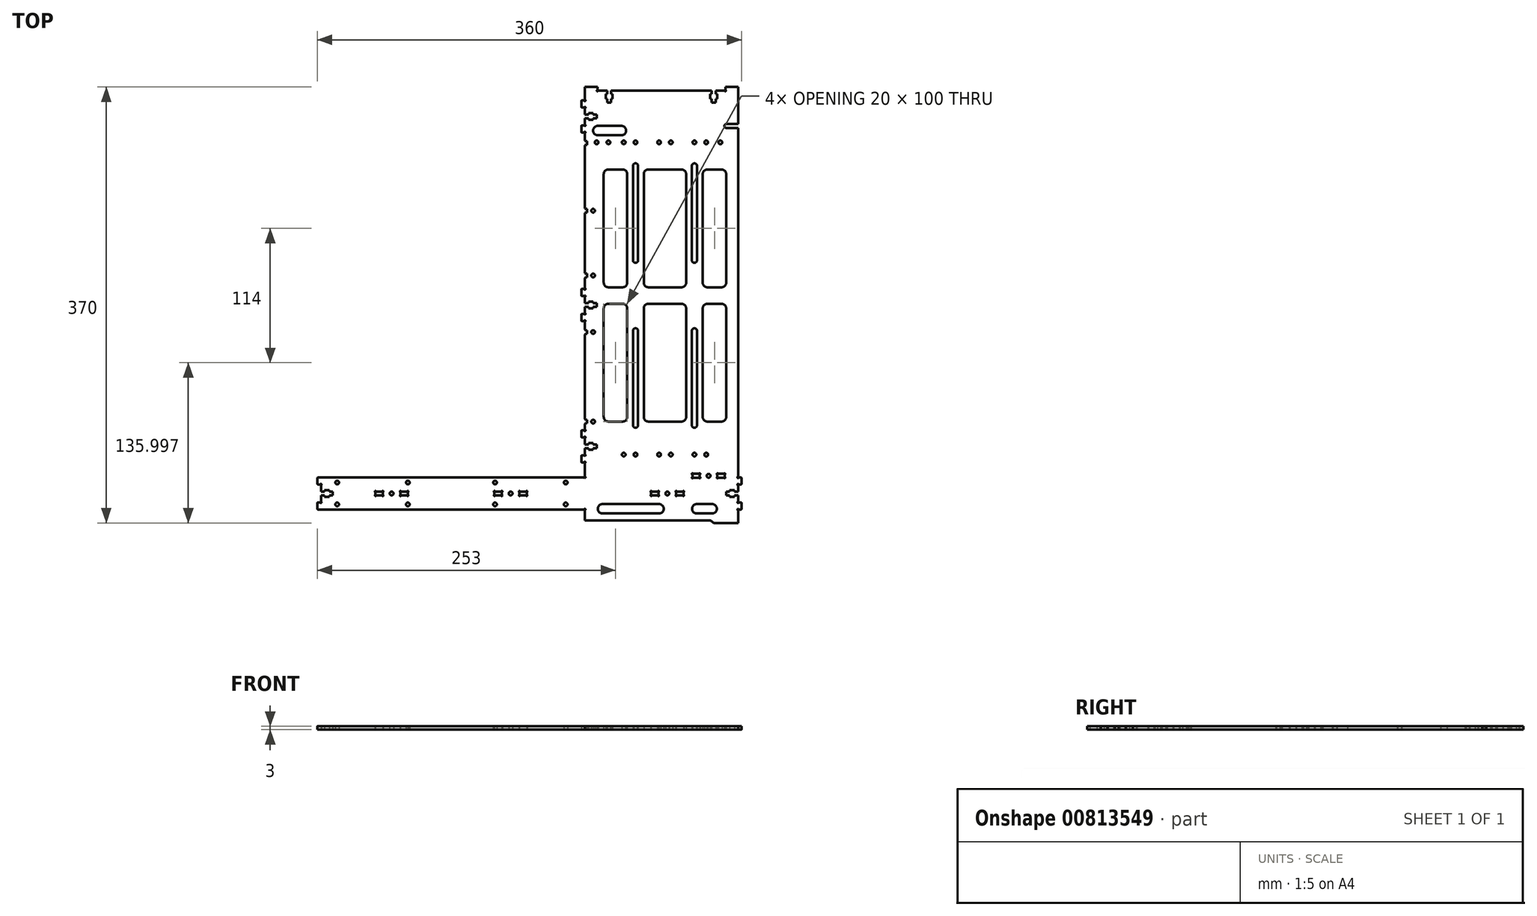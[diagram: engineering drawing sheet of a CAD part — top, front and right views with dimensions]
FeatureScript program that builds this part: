
annotation { "Feature Type Name" : "Feature", "Feature Type Description" : "" }
export const myFeature = defineFeature(function(context is Context, id is Id, definition is map)
    precondition{}
    {
        {
            var Q0;
            Q0=qCreatedBy(makeId("Top.planeOp"),FACE);
            var sketch = newSketch(context, id + "F0", { "sketchPlane" : qUnion([Q0])});
            skCircle(sketch, "E0", {"center": v(30.75, -146.86) * mm, "radius": 1.55 * mm});
            skCircle(sketch, "E1", {"center": v(-103.25, -146.86) * mm, "radius": 1.55 * mm});
            skCircle(sketch, "E2", {"center": v(30.75, -165.45) * mm, "radius": 1.55 * mm});
            skCircle(sketch, "E3", {"center": v(-163.25, -165.45) * mm, "radius": 1.55 * mm});
            skLineSegment(sketch, "E4", {"start": v(-103.3, -156.94) * mm, "end": v(-103.3, -155.37) * mm});
            skArc(sketch, "E5", {"start": v(-103.3, -156.94) * mm, "mid": v(-103.23, -157.19) * mm, "end": v(-103.05, -157.37) * mm});
            skArc(sketch, "E6", {"start": v(-103.73, -158.05) * mm, "mid": v(-102.95, -158.16) * mm, "end": v(-103.05, -157.37) * mm});
            skArc(sketch, "E7", {"start": v(-103.73, -158.05) * mm, "mid": v(-103.92, -157.87) * mm, "end": v(-104.17, -157.8) * mm});
            skLineSegment(sketch, "E8", {"start": v(-108.63, -157.8) * mm, "end": v(-104.17, -157.8) * mm});
            skArc(sketch, "E9", {"start": v(-108.63, -157.8) * mm, "mid": v(-108.88, -157.87) * mm, "end": v(-109.07, -158.05) * mm});
            skArc(sketch, "E10", {"start": v(-109.75, -157.37) * mm, "mid": v(-109.85, -158.16) * mm, "end": v(-109.07, -158.05) * mm});
            skArc(sketch, "E11", {"start": v(-109.75, -157.37) * mm, "mid": v(-109.57, -157.19) * mm, "end": v(-109.5, -156.94) * mm});
            skLineSegment(sketch, "E12", {"start": v(-109.5, -155.37) * mm, "end": v(-109.5, -156.94) * mm});
            skArc(sketch, "E13", {"start": v(-109.5, -155.37) * mm, "mid": v(-109.57, -155.12) * mm, "end": v(-109.75, -154.94) * mm});
            skArc(sketch, "E14", {"start": v(-109.07, -154.25) * mm, "mid": v(-109.85, -154.15) * mm, "end": v(-109.75, -154.94) * mm});
            skArc(sketch, "E15", {"start": v(-109.07, -154.25) * mm, "mid": v(-108.88, -154.44) * mm, "end": v(-108.63, -154.5) * mm});
            skLineSegment(sketch, "E16", {"start": v(-104.17, -154.5) * mm, "end": v(-108.63, -154.5) * mm});
            skArc(sketch, "E17", {"start": v(-104.17, -154.5) * mm, "mid": v(-103.92, -154.44) * mm, "end": v(-103.73, -154.25) * mm});
            skArc(sketch, "E18", {"start": v(-103.05, -154.94) * mm, "mid": v(-102.95, -154.15) * mm, "end": v(-103.73, -154.25) * mm});
            skArc(sketch, "E19", {"start": v(-103.05, -154.94) * mm, "mid": v(-103.23, -155.12) * mm, "end": v(-103.3, -155.37) * mm});
            skLineSegment(sketch, "E20", {"start": v(-124.5, -156.94) * mm, "end": v(-124.5, -155.37) * mm});
            skArc(sketch, "E21", {"start": v(-124.5, -156.94) * mm, "mid": v(-124.43, -157.19) * mm, "end": v(-124.25, -157.37) * mm});
            skArc(sketch, "E22", {"start": v(-124.93, -158.05) * mm, "mid": v(-124.15, -158.16) * mm, "end": v(-124.25, -157.37) * mm});
            skArc(sketch, "E23", {"start": v(-124.93, -158.05) * mm, "mid": v(-125.12, -157.87) * mm, "end": v(-125.37, -157.8) * mm});
            skLineSegment(sketch, "E24", {"start": v(-129.83, -157.8) * mm, "end": v(-125.37, -157.8) * mm});
            skArc(sketch, "E25", {"start": v(-129.83, -157.8) * mm, "mid": v(-130.08, -157.87) * mm, "end": v(-130.27, -158.05) * mm});
            skArc(sketch, "E26", {"start": v(-130.95, -157.37) * mm, "mid": v(-131.05, -158.16) * mm, "end": v(-130.27, -158.05) * mm});
            skArc(sketch, "E27", {"start": v(-130.95, -157.37) * mm, "mid": v(-130.77, -157.19) * mm, "end": v(-130.7, -156.94) * mm});
            skLineSegment(sketch, "E28", {"start": v(-130.7, -155.37) * mm, "end": v(-130.7, -156.94) * mm});
            skArc(sketch, "E29", {"start": v(-130.7, -155.37) * mm, "mid": v(-130.77, -155.12) * mm, "end": v(-130.95, -154.94) * mm});
            skArc(sketch, "E30", {"start": v(-130.27, -154.25) * mm, "mid": v(-131.05, -154.15) * mm, "end": v(-130.95, -154.94) * mm});
            skArc(sketch, "E31", {"start": v(-130.27, -154.25) * mm, "mid": v(-130.08, -154.44) * mm, "end": v(-129.83, -154.5) * mm});
            skLineSegment(sketch, "E32", {"start": v(-125.37, -154.5) * mm, "end": v(-129.83, -154.5) * mm});
            skArc(sketch, "E33", {"start": v(-125.37, -154.5) * mm, "mid": v(-125.12, -154.44) * mm, "end": v(-124.93, -154.25) * mm});
            skArc(sketch, "E34", {"start": v(-124.25, -154.94) * mm, "mid": v(-124.15, -154.15) * mm, "end": v(-124.93, -154.25) * mm});
            skArc(sketch, "E35", {"start": v(-124.25, -154.94) * mm, "mid": v(-124.43, -155.12) * mm, "end": v(-124.5, -155.37) * mm});
            skLineSegment(sketch, "E36", {"start": v(87.8, -18.15) * mm, "end": v(87.8, -98.15) * mm});
            skArc(sketch, "E37", {"start": v(92.2, -18.15) * mm, "mid": v(90, -15.95) * mm, "end": v(87.8, -18.15) * mm});
            skLineSegment(sketch, "E38", {"start": v(92.2, -98.15) * mm, "end": v(92.2, -18.15) * mm});
            skArc(sketch, "E39", {"start": v(87.8, -98.15) * mm, "mid": v(90, -100.35) * mm, "end": v(92.2, -98.15) * mm});
            skLineSegment(sketch, "E40", {"start": v(137.8, -18.15) * mm, "end": v(137.8, -98.15) * mm});
            skArc(sketch, "E41", {"start": v(142.2, -18.15) * mm, "mid": v(140, -15.95) * mm, "end": v(137.8, -18.15) * mm});
            skLineSegment(sketch, "E42", {"start": v(142.2, -98.15) * mm, "end": v(142.2, -18.15) * mm});
            skArc(sketch, "E43", {"start": v(137.8, -98.15) * mm, "mid": v(140, -100.35) * mm, "end": v(142.2, -98.15) * mm});
            skCircle(sketch, "E44", {"center": v(162, 141.85) * mm, "radius": 1.55 * mm});
            skCircle(sketch, "E45", {"center": v(140, 141.85) * mm, "radius": 1.55 * mm});
            skCircle(sketch, "E46", {"center": v(110, 141.85) * mm, "radius": 1.55 * mm});
            skCircle(sketch, "E47", {"center": v(80, 141.85) * mm, "radius": 1.55 * mm});
            skCircle(sketch, "E48", {"center": v(57, 141.85) * mm, "radius": 1.55 * mm});
            skLineSegment(sketch, "E49", {"start": v(165.7, -141.94) * mm, "end": v(165.7, -140.37) * mm});
            skArc(sketch, "E50", {"start": v(165.7, -141.94) * mm, "mid": v(165.77, -142.19) * mm, "end": v(165.95, -142.37) * mm});
            skArc(sketch, "E51", {"start": v(165.27, -143.05) * mm, "mid": v(166.05, -143.16) * mm, "end": v(165.95, -142.37) * mm});
            skArc(sketch, "E52", {"start": v(165.27, -143.05) * mm, "mid": v(165.08, -142.87) * mm, "end": v(164.83, -142.8) * mm});
            skLineSegment(sketch, "E53", {"start": v(160.37, -142.8) * mm, "end": v(164.83, -142.8) * mm});
            skArc(sketch, "E54", {"start": v(160.37, -142.8) * mm, "mid": v(160.12, -142.87) * mm, "end": v(159.93, -143.05) * mm});
            skArc(sketch, "E55", {"start": v(159.25, -142.37) * mm, "mid": v(159.15, -143.16) * mm, "end": v(159.93, -143.05) * mm});
            skArc(sketch, "E56", {"start": v(159.25, -142.37) * mm, "mid": v(159.43, -142.19) * mm, "end": v(159.5, -141.94) * mm});
            skLineSegment(sketch, "E57", {"start": v(159.5, -140.37) * mm, "end": v(159.5, -141.94) * mm});
            skArc(sketch, "E58", {"start": v(159.5, -140.37) * mm, "mid": v(159.43, -140.12) * mm, "end": v(159.25, -139.94) * mm});
            skArc(sketch, "E59", {"start": v(159.93, -139.25) * mm, "mid": v(159.15, -139.15) * mm, "end": v(159.25, -139.94) * mm});
            skArc(sketch, "E60", {"start": v(159.93, -139.25) * mm, "mid": v(160.12, -139.44) * mm, "end": v(160.37, -139.5) * mm});
            skLineSegment(sketch, "E61", {"start": v(164.83, -139.5) * mm, "end": v(160.37, -139.5) * mm});
            skArc(sketch, "E62", {"start": v(164.83, -139.5) * mm, "mid": v(165.08, -139.44) * mm, "end": v(165.27, -139.25) * mm});
            skArc(sketch, "E63", {"start": v(165.95, -139.94) * mm, "mid": v(166.05, -139.15) * mm, "end": v(165.27, -139.25) * mm});
            skArc(sketch, "E64", {"start": v(165.95, -139.94) * mm, "mid": v(165.77, -140.12) * mm, "end": v(165.7, -140.37) * mm});
            skLineSegment(sketch, "E65", {"start": v(144.5, -141.94) * mm, "end": v(144.5, -140.37) * mm});
            skArc(sketch, "E66", {"start": v(144.5, -141.94) * mm, "mid": v(144.57, -142.19) * mm, "end": v(144.75, -142.37) * mm});
            skArc(sketch, "E67", {"start": v(144.07, -143.05) * mm, "mid": v(144.85, -143.16) * mm, "end": v(144.75, -142.37) * mm});
            skArc(sketch, "E68", {"start": v(144.07, -143.05) * mm, "mid": v(143.88, -142.87) * mm, "end": v(143.63, -142.8) * mm});
            skLineSegment(sketch, "E69", {"start": v(139.17, -142.8) * mm, "end": v(143.63, -142.8) * mm});
            skArc(sketch, "E70", {"start": v(139.17, -142.8) * mm, "mid": v(138.92, -142.87) * mm, "end": v(138.73, -143.05) * mm});
            skArc(sketch, "E71", {"start": v(138.05, -142.37) * mm, "mid": v(137.95, -143.16) * mm, "end": v(138.73, -143.05) * mm});
            skArc(sketch, "E72", {"start": v(138.05, -142.37) * mm, "mid": v(138.23, -142.19) * mm, "end": v(138.3, -141.94) * mm});
            skLineSegment(sketch, "E73", {"start": v(138.3, -140.37) * mm, "end": v(138.3, -141.94) * mm});
            skArc(sketch, "E74", {"start": v(138.3, -140.37) * mm, "mid": v(138.23, -140.12) * mm, "end": v(138.05, -139.94) * mm});
            skArc(sketch, "E75", {"start": v(138.73, -139.25) * mm, "mid": v(137.95, -139.15) * mm, "end": v(138.05, -139.94) * mm});
            skArc(sketch, "E76", {"start": v(138.73, -139.25) * mm, "mid": v(138.92, -139.44) * mm, "end": v(139.17, -139.5) * mm});
            skLineSegment(sketch, "E77", {"start": v(143.63, -139.5) * mm, "end": v(139.17, -139.5) * mm});
            skArc(sketch, "E78", {"start": v(143.63, -139.5) * mm, "mid": v(143.88, -139.44) * mm, "end": v(144.07, -139.25) * mm});
            skArc(sketch, "E79", {"start": v(144.75, -139.94) * mm, "mid": v(144.85, -139.15) * mm, "end": v(144.07, -139.25) * mm});
            skArc(sketch, "E80", {"start": v(144.75, -139.94) * mm, "mid": v(144.57, -140.12) * mm, "end": v(144.5, -140.37) * mm});
            skCircle(sketch, "E81", {"center": v(117, -156.15) * mm, "radius": 1.6 * mm});
            skCircle(sketch, "E82", {"center": v(80, -123.15) * mm, "radius": 1.55 * mm});
            skCircle(sketch, "E83", {"center": v(140, -123.15) * mm, "radius": 1.55 * mm});
            skCircle(sketch, "E84", {"center": v(110, -123.15) * mm, "radius": 1.55 * mm});
            skCircle(sketch, "E85", {"center": v(54, -95.15) * mm, "radius": 1.55 * mm});
            skCircle(sketch, "E86", {"center": v(54, 28.85) * mm, "radius": 1.55 * mm});
            skLineSegment(sketch, "E87", {"start": v(-2.3, -156.94) * mm, "end": v(-2.3, -155.37) * mm});
            skArc(sketch, "E88", {"start": v(-2.3, -156.94) * mm, "mid": v(-2.23, -157.19) * mm, "end": v(-2.05, -157.37) * mm});
            skArc(sketch, "E89", {"start": v(-2.73, -158.05) * mm, "mid": v(-1.95, -158.16) * mm, "end": v(-2.05, -157.37) * mm});
            skArc(sketch, "E90", {"start": v(-2.73, -158.05) * mm, "mid": v(-2.92, -157.87) * mm, "end": v(-3.17, -157.8) * mm});
            skLineSegment(sketch, "E91", {"start": v(-7.63, -157.8) * mm, "end": v(-3.17, -157.8) * mm});
            skArc(sketch, "E92", {"start": v(-7.63, -157.8) * mm, "mid": v(-7.88, -157.87) * mm, "end": v(-8.07, -158.05) * mm});
            skArc(sketch, "E93", {"start": v(-8.75, -157.37) * mm, "mid": v(-8.85, -158.16) * mm, "end": v(-8.07, -158.05) * mm});
            skArc(sketch, "E94", {"start": v(-8.75, -157.37) * mm, "mid": v(-8.57, -157.19) * mm, "end": v(-8.5, -156.94) * mm});
            skLineSegment(sketch, "E95", {"start": v(-8.5, -155.37) * mm, "end": v(-8.5, -156.94) * mm});
            skArc(sketch, "E96", {"start": v(-8.5, -155.37) * mm, "mid": v(-8.57, -155.12) * mm, "end": v(-8.75, -154.94) * mm});
            skArc(sketch, "E97", {"start": v(-8.07, -154.25) * mm, "mid": v(-8.85, -154.15) * mm, "end": v(-8.75, -154.94) * mm});
            skArc(sketch, "E98", {"start": v(-8.07, -154.25) * mm, "mid": v(-7.88, -154.44) * mm, "end": v(-7.63, -154.5) * mm});
            skLineSegment(sketch, "E99", {"start": v(-3.17, -154.5) * mm, "end": v(-7.63, -154.5) * mm});
            skArc(sketch, "E100", {"start": v(-3.17, -154.5) * mm, "mid": v(-2.92, -154.44) * mm, "end": v(-2.73, -154.25) * mm});
            skArc(sketch, "E101", {"start": v(-2.05, -154.94) * mm, "mid": v(-1.95, -154.15) * mm, "end": v(-2.73, -154.25) * mm});
            skArc(sketch, "E102", {"start": v(-2.05, -154.94) * mm, "mid": v(-2.23, -155.12) * mm, "end": v(-2.3, -155.37) * mm});
            skLineSegment(sketch, "E103", {"start": v(-23.5, -156.94) * mm, "end": v(-23.5, -155.37) * mm});
            skArc(sketch, "E104", {"start": v(-23.5, -156.94) * mm, "mid": v(-23.43, -157.19) * mm, "end": v(-23.25, -157.37) * mm});
            skArc(sketch, "E105", {"start": v(-23.93, -158.05) * mm, "mid": v(-23.15, -158.16) * mm, "end": v(-23.25, -157.37) * mm});
            skArc(sketch, "E106", {"start": v(-23.93, -158.05) * mm, "mid": v(-24.12, -157.87) * mm, "end": v(-24.37, -157.8) * mm});
            skLineSegment(sketch, "E107", {"start": v(-28.83, -157.8) * mm, "end": v(-24.37, -157.8) * mm});
            skArc(sketch, "E108", {"start": v(-28.83, -157.8) * mm, "mid": v(-29.08, -157.87) * mm, "end": v(-29.27, -158.05) * mm});
            skArc(sketch, "E109", {"start": v(-29.95, -157.37) * mm, "mid": v(-30.05, -158.16) * mm, "end": v(-29.27, -158.05) * mm});
            skArc(sketch, "E110", {"start": v(-29.95, -157.37) * mm, "mid": v(-29.77, -157.19) * mm, "end": v(-29.7, -156.94) * mm});
            skLineSegment(sketch, "E111", {"start": v(-29.7, -155.37) * mm, "end": v(-29.7, -156.94) * mm});
            skArc(sketch, "E112", {"start": v(-29.7, -155.37) * mm, "mid": v(-29.77, -155.12) * mm, "end": v(-29.95, -154.94) * mm});
            skArc(sketch, "E113", {"start": v(-29.27, -154.25) * mm, "mid": v(-30.05, -154.15) * mm, "end": v(-29.95, -154.94) * mm});
            skArc(sketch, "E114", {"start": v(-29.27, -154.25) * mm, "mid": v(-29.08, -154.44) * mm, "end": v(-28.83, -154.5) * mm});
            skLineSegment(sketch, "E115", {"start": v(-24.37, -154.5) * mm, "end": v(-28.83, -154.5) * mm});
            skArc(sketch, "E116", {"start": v(-24.37, -154.5) * mm, "mid": v(-24.12, -154.44) * mm, "end": v(-23.93, -154.25) * mm});
            skArc(sketch, "E117", {"start": v(-23.25, -154.94) * mm, "mid": v(-23.15, -154.15) * mm, "end": v(-23.93, -154.25) * mm});
            skArc(sketch, "E118", {"start": v(-23.25, -154.94) * mm, "mid": v(-23.43, -155.12) * mm, "end": v(-23.5, -155.37) * mm});
            skLineSegment(sketch, "E119", {"start": v(62, -173.15) * mm, "end": v(110, -173.15) * mm});
            skArc(sketch, "E120", {"start": v(62, -165.15) * mm, "mid": v(58, -169.15) * mm, "end": v(62, -173.15) * mm});
            skLineSegment(sketch, "E121", {"start": v(110, -165.15) * mm, "end": v(62, -165.15) * mm});
            skArc(sketch, "E122", {"start": v(110, -173.15) * mm, "mid": v(114, -169.15) * mm, "end": v(110, -165.15) * mm});
            skArc(sketch, "E123", {"start": v(47.25, -170.19) * mm, "mid": v(47.35, -169.4) * mm, "end": v(46.57, -169.5) * mm});
            skArc(sketch, "E124", {"start": v(47.25, -170.19) * mm, "mid": v(47.07, -170.37) * mm, "end": v(47, -170.62) * mm});
            skLineSegment(sketch, "E125", {"start": v(47, -170.62) * mm, "end": v(47, -179.15) * mm});
            skLineSegment(sketch, "E126", {"start": v(47, -179.15) * mm, "end": v(153.17, -179.15) * mm});
            skArc(sketch, "E127", {"start": v(154.59, -179.74) * mm, "mid": v(153.94, -179.3) * mm, "end": v(153.17, -179.15) * mm});
            skLineSegment(sketch, "E128", {"start": v(154.59, -179.74) * mm, "end": v(155.41, -180.57) * mm});
            skArc(sketch, "E129", {"start": v(155.41, -180.57) * mm, "mid": v(156.06, -181) * mm, "end": v(156.83, -181.15) * mm});
            skLineSegment(sketch, "E130", {"start": v(156.83, -181.15) * mm, "end": v(177, -181.15) * mm});
            skLineSegment(sketch, "E131", {"start": v(177, -181.15) * mm, "end": v(177, -170.62) * mm});
            skArc(sketch, "E132", {"start": v(177, -170.62) * mm, "mid": v(176.93, -170.37) * mm, "end": v(176.75, -170.19) * mm});
            skArc(sketch, "E133", {"start": v(177.43, -169.5) * mm, "mid": v(176.65, -169.4) * mm, "end": v(176.75, -170.19) * mm});
            skArc(sketch, "E134", {"start": v(177.43, -169.5) * mm, "mid": v(177.62, -169.69) * mm, "end": v(177.87, -169.75) * mm});
            skLineSegment(sketch, "E135", {"start": v(177.87, -169.75) * mm, "end": v(179.5, -169.75) * mm});
            skArc(sketch, "E136", {"start": v(179.5, -169.75) * mm, "mid": v(179.85, -169.6) * mm, "end": v(180, -169.25) * mm});
            skLineSegment(sketch, "E137", {"start": v(180, -169.25) * mm, "end": v(180, -164.25) * mm});
            skArc(sketch, "E138", {"start": v(180, -164.25) * mm, "mid": v(179.85, -163.9) * mm, "end": v(179.5, -163.75) * mm});
            skLineSegment(sketch, "E139", {"start": v(179.5, -163.75) * mm, "end": v(177.87, -163.75) * mm});
            skArc(sketch, "E140", {"start": v(177.87, -163.75) * mm, "mid": v(177.62, -163.82) * mm, "end": v(177.43, -164) * mm});
            skArc(sketch, "E141", {"start": v(176.75, -163.32) * mm, "mid": v(176.65, -164.1) * mm, "end": v(177.43, -164) * mm});
            skArc(sketch, "E142", {"start": v(176.75, -163.32) * mm, "mid": v(176.93, -163.14) * mm, "end": v(177, -162.89) * mm});
            skLineSegment(sketch, "E143", {"start": v(177, -162.89) * mm, "end": v(177, -157.75) * mm});
            skLineSegment(sketch, "E144", {"start": v(177, -157.75) * mm, "end": v(174, -157.75) * mm});
            skLineSegment(sketch, "E145", {"start": v(174, -157.75) * mm, "end": v(174, -159.03) * mm});
            skLineSegment(sketch, "E146", {"start": v(174, -159.03) * mm, "end": v(170, -159.03) * mm});
            skLineSegment(sketch, "E147", {"start": v(170, -159.03) * mm, "end": v(170, -157.75) * mm});
            skLineSegment(sketch, "E148", {"start": v(170, -157.75) * mm, "end": v(167, -157.75) * mm});
            skLineSegment(sketch, "E149", {"start": v(167, -157.75) * mm, "end": v(167, -154.55) * mm});
            skLineSegment(sketch, "E150", {"start": v(167, -154.55) * mm, "end": v(170, -154.55) * mm});
            skLineSegment(sketch, "E151", {"start": v(170, -154.55) * mm, "end": v(170, -153.28) * mm});
            skLineSegment(sketch, "E152", {"start": v(170, -153.28) * mm, "end": v(174, -153.28) * mm});
            skLineSegment(sketch, "E153", {"start": v(174, -153.28) * mm, "end": v(174, -154.55) * mm});
            skLineSegment(sketch, "E154", {"start": v(174, -154.55) * mm, "end": v(177, -154.55) * mm});
            skLineSegment(sketch, "E155", {"start": v(177, -154.55) * mm, "end": v(177, -149.42) * mm});
            skArc(sketch, "E156", {"start": v(177, -149.42) * mm, "mid": v(176.93, -149.17) * mm, "end": v(176.75, -148.99) * mm});
            skArc(sketch, "E157", {"start": v(177.43, -148.3) * mm, "mid": v(176.65, -148.2) * mm, "end": v(176.75, -148.99) * mm});
            skArc(sketch, "E158", {"start": v(177.43, -148.3) * mm, "mid": v(177.62, -148.49) * mm, "end": v(177.87, -148.55) * mm});
            skLineSegment(sketch, "E159", {"start": v(177.87, -148.55) * mm, "end": v(179.5, -148.55) * mm});
            skArc(sketch, "E160", {"start": v(179.5, -148.55) * mm, "mid": v(179.85, -148.4) * mm, "end": v(180, -148.05) * mm});
            skLineSegment(sketch, "E161", {"start": v(180, -148.05) * mm, "end": v(180, -143.05) * mm});
            skArc(sketch, "E162", {"start": v(180, -143.05) * mm, "mid": v(179.85, -142.7) * mm, "end": v(179.5, -142.55) * mm});
            skLineSegment(sketch, "E163", {"start": v(179.5, -142.55) * mm, "end": v(177.87, -142.55) * mm});
            skArc(sketch, "E164", {"start": v(177.87, -142.55) * mm, "mid": v(177.62, -142.62) * mm, "end": v(177.43, -142.8) * mm});
            skArc(sketch, "E165", {"start": v(176.75, -142.12) * mm, "mid": v(176.65, -142.9) * mm, "end": v(177.43, -142.8) * mm});
            skArc(sketch, "E166", {"start": v(176.75, -142.12) * mm, "mid": v(176.93, -141.94) * mm, "end": v(177, -141.69) * mm});
            skLineSegment(sketch, "E167", {"start": v(177, -141.69) * mm, "end": v(177, 153.9) * mm});
            skLineSegment(sketch, "E168", {"start": v(177, 153.9) * mm, "end": v(176.75, 154.15) * mm});
            skLineSegment(sketch, "E169", {"start": v(176.75, 154.15) * mm, "end": v(167, 154.15) * mm});
            skArc(sketch, "E170", {"start": v(167, 157.35) * mm, "mid": v(165.4, 155.75) * mm, "end": v(167, 154.15) * mm});
            skLineSegment(sketch, "E171", {"start": v(167, 157.35) * mm, "end": v(176.75, 157.35) * mm});
            skLineSegment(sketch, "E172", {"start": v(176.75, 157.35) * mm, "end": v(177, 157.6) * mm});
            skLineSegment(sketch, "E173", {"start": v(177, 157.6) * mm, "end": v(177, 188.85) * mm});
            skLineSegment(sketch, "E174", {"start": v(177, 188.85) * mm, "end": v(166.35, 188.85) * mm});
            skLineSegment(sketch, "E175", {"start": v(166.35, 188.85) * mm, "end": v(166.35, 186.61) * mm});
            skArc(sketch, "E176", {"start": v(166.35, 186.61) * mm, "mid": v(166.42, 186.36) * mm, "end": v(166.6, 186.18) * mm});
            skArc(sketch, "E177", {"start": v(165.92, 185.5) * mm, "mid": v(166.7, 185.4) * mm, "end": v(166.6, 186.18) * mm});
            skArc(sketch, "E178", {"start": v(165.92, 185.5) * mm, "mid": v(165.73, 185.68) * mm, "end": v(165.48, 185.75) * mm});
            skLineSegment(sketch, "E179", {"start": v(165.48, 185.75) * mm, "end": v(157.95, 185.75) * mm});
            skLineSegment(sketch, "E180", {"start": v(157.95, 185.75) * mm, "end": v(157.95, 182.75) * mm});
            skLineSegment(sketch, "E181", {"start": v(157.95, 182.75) * mm, "end": v(159.22, 182.75) * mm});
            skLineSegment(sketch, "E182", {"start": v(159.22, 182.75) * mm, "end": v(159.22, 178.75) * mm});
            skLineSegment(sketch, "E183", {"start": v(159.22, 178.75) * mm, "end": v(157.95, 178.75) * mm});
            skLineSegment(sketch, "E184", {"start": v(157.95, 178.75) * mm, "end": v(157.95, 175.75) * mm});
            skLineSegment(sketch, "E185", {"start": v(157.95, 175.75) * mm, "end": v(154.75, 175.75) * mm});
            skLineSegment(sketch, "E186", {"start": v(154.75, 175.75) * mm, "end": v(154.75, 178.75) * mm});
            skLineSegment(sketch, "E187", {"start": v(154.75, 178.75) * mm, "end": v(153.47, 178.75) * mm});
            skLineSegment(sketch, "E188", {"start": v(153.47, 178.75) * mm, "end": v(153.47, 182.75) * mm});
            skLineSegment(sketch, "E189", {"start": v(153.47, 182.75) * mm, "end": v(154.75, 182.75) * mm});
            skLineSegment(sketch, "E190", {"start": v(154.75, 182.75) * mm, "end": v(154.75, 185.75) * mm});
            skLineSegment(sketch, "E191", {"start": v(154.75, 185.75) * mm, "end": v(69.25, 185.75) * mm});
            skLineSegment(sketch, "E192", {"start": v(69.25, 185.75) * mm, "end": v(69.25, 182.75) * mm});
            skLineSegment(sketch, "E193", {"start": v(69.25, 182.75) * mm, "end": v(70.53, 182.75) * mm});
            skLineSegment(sketch, "E194", {"start": v(70.53, 182.75) * mm, "end": v(70.53, 178.75) * mm});
            skLineSegment(sketch, "E195", {"start": v(70.53, 178.75) * mm, "end": v(69.25, 178.75) * mm});
            skLineSegment(sketch, "E196", {"start": v(69.25, 178.75) * mm, "end": v(69.25, 175.75) * mm});
            skLineSegment(sketch, "E197", {"start": v(69.25, 175.75) * mm, "end": v(66.05, 175.75) * mm});
            skLineSegment(sketch, "E198", {"start": v(66.05, 175.75) * mm, "end": v(66.05, 178.75) * mm});
            skLineSegment(sketch, "E199", {"start": v(66.05, 178.75) * mm, "end": v(64.78, 178.75) * mm});
            skLineSegment(sketch, "E200", {"start": v(64.78, 178.75) * mm, "end": v(64.78, 182.75) * mm});
            skLineSegment(sketch, "E201", {"start": v(64.78, 182.75) * mm, "end": v(66.05, 182.75) * mm});
            skLineSegment(sketch, "E202", {"start": v(66.05, 182.75) * mm, "end": v(66.05, 185.75) * mm});
            skLineSegment(sketch, "E203", {"start": v(66.05, 185.75) * mm, "end": v(58.52, 185.75) * mm});
            skArc(sketch, "E204", {"start": v(58.52, 185.75) * mm, "mid": v(58.27, 185.68) * mm, "end": v(58.08, 185.5) * mm});
            skArc(sketch, "E205", {"start": v(57.4, 186.18) * mm, "mid": v(57.3, 185.4) * mm, "end": v(58.08, 185.5) * mm});
            skArc(sketch, "E206", {"start": v(57.4, 186.18) * mm, "mid": v(57.58, 186.36) * mm, "end": v(57.65, 186.61) * mm});
            skLineSegment(sketch, "E207", {"start": v(57.65, 186.61) * mm, "end": v(57.65, 188.85) * mm});
            skLineSegment(sketch, "E208", {"start": v(57.65, 188.85) * mm, "end": v(47, 188.85) * mm});
            skLineSegment(sketch, "E209", {"start": v(47, 188.85) * mm, "end": v(47, 178.31) * mm});
            skArc(sketch, "E210", {"start": v(47, 178.31) * mm, "mid": v(47.07, 178.06) * mm, "end": v(47.25, 177.88) * mm});
            skArc(sketch, "E211", {"start": v(46.57, 177.2) * mm, "mid": v(47.35, 177.1) * mm, "end": v(47.25, 177.88) * mm});
            skArc(sketch, "E212", {"start": v(46.57, 177.2) * mm, "mid": v(46.38, 177.38) * mm, "end": v(46.13, 177.45) * mm});
            skLineSegment(sketch, "E213", {"start": v(46.13, 177.45) * mm, "end": v(44.5, 177.45) * mm});
            skArc(sketch, "E214", {"start": v(44.5, 177.45) * mm, "mid": v(44.15, 177.3) * mm, "end": v(44, 176.95) * mm});
            skLineSegment(sketch, "E215", {"start": v(44, 176.95) * mm, "end": v(44, 171.95) * mm});
            skArc(sketch, "E216", {"start": v(44, 171.95) * mm, "mid": v(44.15, 171.6) * mm, "end": v(44.5, 171.45) * mm});
            skLineSegment(sketch, "E217", {"start": v(44.5, 171.45) * mm, "end": v(46.13, 171.45) * mm});
            skArc(sketch, "E218", {"start": v(46.13, 171.45) * mm, "mid": v(46.38, 171.51) * mm, "end": v(46.57, 171.7) * mm});
            skArc(sketch, "E219", {"start": v(47.25, 171.01) * mm, "mid": v(47.35, 171.8) * mm, "end": v(46.57, 171.7) * mm});
            skArc(sketch, "E220", {"start": v(47.25, 171.01) * mm, "mid": v(47.07, 170.83) * mm, "end": v(47, 170.58) * mm});
            skLineSegment(sketch, "E221", {"start": v(47, 170.58) * mm, "end": v(47, 165.45) * mm});
            skLineSegment(sketch, "E222", {"start": v(47, 165.45) * mm, "end": v(50, 165.45) * mm});
            skLineSegment(sketch, "E223", {"start": v(50, 165.45) * mm, "end": v(50, 166.72) * mm});
            skLineSegment(sketch, "E224", {"start": v(50, 166.72) * mm, "end": v(54, 166.72) * mm});
            skLineSegment(sketch, "E225", {"start": v(54, 166.72) * mm, "end": v(54, 165.45) * mm});
            skLineSegment(sketch, "E226", {"start": v(54, 165.45) * mm, "end": v(57, 165.45) * mm});
            skLineSegment(sketch, "E227", {"start": v(57, 165.45) * mm, "end": v(57, 162.25) * mm});
            skLineSegment(sketch, "E228", {"start": v(57, 162.25) * mm, "end": v(54, 162.25) * mm});
            skLineSegment(sketch, "E229", {"start": v(54, 162.25) * mm, "end": v(54, 160.97) * mm});
            skLineSegment(sketch, "E230", {"start": v(54, 160.97) * mm, "end": v(50, 160.97) * mm});
            skLineSegment(sketch, "E231", {"start": v(50, 160.97) * mm, "end": v(50, 162.25) * mm});
            skLineSegment(sketch, "E232", {"start": v(50, 162.25) * mm, "end": v(47, 162.25) * mm});
            skLineSegment(sketch, "E233", {"start": v(47, 162.25) * mm, "end": v(47, 157.11) * mm});
            skArc(sketch, "E234", {"start": v(47, 157.11) * mm, "mid": v(47.07, 156.86) * mm, "end": v(47.25, 156.68) * mm});
            skArc(sketch, "E235", {"start": v(46.57, 156) * mm, "mid": v(47.35, 155.9) * mm, "end": v(47.25, 156.68) * mm});
            skArc(sketch, "E236", {"start": v(46.57, 156) * mm, "mid": v(46.38, 156.18) * mm, "end": v(46.13, 156.25) * mm});
            skLineSegment(sketch, "E237", {"start": v(46.13, 156.25) * mm, "end": v(44.5, 156.25) * mm});
            skArc(sketch, "E238", {"start": v(44.5, 156.25) * mm, "mid": v(44.15, 156.1) * mm, "end": v(44, 155.75) * mm});
            skLineSegment(sketch, "E239", {"start": v(44, 155.75) * mm, "end": v(44, 150.75) * mm});
            skArc(sketch, "E240", {"start": v(44, 150.75) * mm, "mid": v(44.15, 150.4) * mm, "end": v(44.5, 150.25) * mm});
            skLineSegment(sketch, "E241", {"start": v(44.5, 150.25) * mm, "end": v(46.13, 150.25) * mm});
            skArc(sketch, "E242", {"start": v(46.13, 150.25) * mm, "mid": v(46.38, 150.31) * mm, "end": v(46.57, 150.5) * mm});
            skArc(sketch, "E243", {"start": v(47.25, 149.81) * mm, "mid": v(47.35, 150.6) * mm, "end": v(46.57, 150.5) * mm});
            skArc(sketch, "E244", {"start": v(47.25, 149.81) * mm, "mid": v(47.07, 149.63) * mm, "end": v(47, 149.38) * mm});
            skLineSegment(sketch, "E245", {"start": v(47, 149.38) * mm, "end": v(47, 143.35) * mm});
            skLineSegment(sketch, "E246", {"start": v(47, 143.35) * mm, "end": v(47.5, 142.85) * mm});
            skLineSegment(sketch, "E247", {"start": v(47.5, 142.85) * mm, "end": v(49, 142.85) * mm});
            skLineSegment(sketch, "E248", {"start": v(49, 142.85) * mm, "end": v(49, 139.85) * mm});
            skLineSegment(sketch, "E249", {"start": v(49, 139.85) * mm, "end": v(47.5, 139.85) * mm});
            skLineSegment(sketch, "E250", {"start": v(47.5, 139.85) * mm, "end": v(47, 139.35) * mm});
            skLineSegment(sketch, "E251", {"start": v(47, 139.35) * mm, "end": v(47, 85.85) * mm});
            skLineSegment(sketch, "E252", {"start": v(47, 85.85) * mm, "end": v(47.5, 85.35) * mm});
            skLineSegment(sketch, "E253", {"start": v(47.5, 85.35) * mm, "end": v(49, 85.35) * mm});
            skLineSegment(sketch, "E254", {"start": v(49, 85.35) * mm, "end": v(49, 82.35) * mm});
            skLineSegment(sketch, "E255", {"start": v(49, 82.35) * mm, "end": v(47.5, 82.35) * mm});
            skLineSegment(sketch, "E256", {"start": v(47.5, 82.35) * mm, "end": v(47, 81.85) * mm});
            skLineSegment(sketch, "E257", {"start": v(47, 81.85) * mm, "end": v(47, 30.85) * mm});
            skLineSegment(sketch, "E258", {"start": v(47, 30.85) * mm, "end": v(47.5, 30.35) * mm});
            skLineSegment(sketch, "E259", {"start": v(47.5, 30.35) * mm, "end": v(49, 30.35) * mm});
            skLineSegment(sketch, "E260", {"start": v(49, 30.35) * mm, "end": v(49, 27.35) * mm});
            skLineSegment(sketch, "E261", {"start": v(49, 27.35) * mm, "end": v(47.5, 27.35) * mm});
            skLineSegment(sketch, "E262", {"start": v(47.5, 27.35) * mm, "end": v(47, 26.85) * mm});
            skLineSegment(sketch, "E263", {"start": v(47, 26.85) * mm, "end": v(47, 18.31) * mm});
            skArc(sketch, "E264", {"start": v(47, 18.31) * mm, "mid": v(47.07, 18.06) * mm, "end": v(47.25, 17.88) * mm});
            skArc(sketch, "E265", {"start": v(46.57, 17.2) * mm, "mid": v(47.35, 17.1) * mm, "end": v(47.25, 17.88) * mm});
            skArc(sketch, "E266", {"start": v(46.57, 17.2) * mm, "mid": v(46.38, 17.38) * mm, "end": v(46.13, 17.45) * mm});
            skLineSegment(sketch, "E267", {"start": v(46.13, 17.45) * mm, "end": v(44.5, 17.45) * mm});
            skArc(sketch, "E268", {"start": v(44.5, 17.45) * mm, "mid": v(44.15, 17.3) * mm, "end": v(44, 16.95) * mm});
            skLineSegment(sketch, "E269", {"start": v(44, 16.95) * mm, "end": v(44, 11.95) * mm});
            skArc(sketch, "E270", {"start": v(44, 11.95) * mm, "mid": v(44.15, 11.6) * mm, "end": v(44.5, 11.45) * mm});
            skLineSegment(sketch, "E271", {"start": v(44.5, 11.45) * mm, "end": v(46.13, 11.45) * mm});
            skArc(sketch, "E272", {"start": v(46.13, 11.45) * mm, "mid": v(46.38, 11.51) * mm, "end": v(46.57, 11.7) * mm});
            skArc(sketch, "E273", {"start": v(47.25, 11.01) * mm, "mid": v(47.35, 11.8) * mm, "end": v(46.57, 11.7) * mm});
            skArc(sketch, "E274", {"start": v(47.25, 11.01) * mm, "mid": v(47.07, 10.83) * mm, "end": v(47, 10.58) * mm});
            skLineSegment(sketch, "E275", {"start": v(47, 10.58) * mm, "end": v(47, 5.45) * mm});
            skLineSegment(sketch, "E276", {"start": v(47, 5.45) * mm, "end": v(50, 5.45) * mm});
            skLineSegment(sketch, "E277", {"start": v(50, 5.45) * mm, "end": v(50, 6.72) * mm});
            skLineSegment(sketch, "E278", {"start": v(50, 6.72) * mm, "end": v(54, 6.72) * mm});
            skLineSegment(sketch, "E279", {"start": v(54, 6.72) * mm, "end": v(54, 5.45) * mm});
            skLineSegment(sketch, "E280", {"start": v(54, 5.45) * mm, "end": v(57, 5.45) * mm});
            skLineSegment(sketch, "E281", {"start": v(57, 5.45) * mm, "end": v(57, 2.25) * mm});
            skLineSegment(sketch, "E282", {"start": v(57, 2.25) * mm, "end": v(54, 2.25) * mm});
            skLineSegment(sketch, "E283", {"start": v(54, 2.25) * mm, "end": v(54, 0.97) * mm});
            skLineSegment(sketch, "E284", {"start": v(54, 0.97) * mm, "end": v(50, 0.97) * mm});
            skLineSegment(sketch, "E285", {"start": v(50, 0.97) * mm, "end": v(50, 2.25) * mm});
            skLineSegment(sketch, "E286", {"start": v(50, 2.25) * mm, "end": v(47, 2.25) * mm});
            skLineSegment(sketch, "E287", {"start": v(47, 2.25) * mm, "end": v(47, -2.89) * mm});
            skArc(sketch, "E288", {"start": v(47, -2.89) * mm, "mid": v(47.07, -3.14) * mm, "end": v(47.25, -3.32) * mm});
            skArc(sketch, "E289", {"start": v(46.57, -4) * mm, "mid": v(47.35, -4.1) * mm, "end": v(47.25, -3.32) * mm});
            skArc(sketch, "E290", {"start": v(46.57, -4) * mm, "mid": v(46.38, -3.82) * mm, "end": v(46.13, -3.75) * mm});
            skLineSegment(sketch, "E291", {"start": v(46.13, -3.75) * mm, "end": v(44.5, -3.75) * mm});
            skArc(sketch, "E292", {"start": v(44.5, -3.75) * mm, "mid": v(44.15, -3.9) * mm, "end": v(44, -4.25) * mm});
            skLineSegment(sketch, "E293", {"start": v(44, -4.25) * mm, "end": v(44, -9.25) * mm});
            skArc(sketch, "E294", {"start": v(44, -9.25) * mm, "mid": v(44.15, -9.6) * mm, "end": v(44.5, -9.75) * mm});
            skLineSegment(sketch, "E295", {"start": v(44.5, -9.75) * mm, "end": v(46.13, -9.75) * mm});
            skArc(sketch, "E296", {"start": v(46.13, -9.75) * mm, "mid": v(46.38, -9.69) * mm, "end": v(46.57, -9.5) * mm});
            skArc(sketch, "E297", {"start": v(47.25, -10.19) * mm, "mid": v(47.35, -9.4) * mm, "end": v(46.57, -9.5) * mm});
            skArc(sketch, "E298", {"start": v(47.25, -10.19) * mm, "mid": v(47.07, -10.37) * mm, "end": v(47, -10.62) * mm});
            skLineSegment(sketch, "E299", {"start": v(47, -10.62) * mm, "end": v(47, -17.15) * mm});
            skLineSegment(sketch, "E300", {"start": v(47, -17.15) * mm, "end": v(47.5, -17.65) * mm});
            skLineSegment(sketch, "E301", {"start": v(47.5, -17.65) * mm, "end": v(49, -17.65) * mm});
            skLineSegment(sketch, "E302", {"start": v(49, -17.65) * mm, "end": v(49, -20.65) * mm});
            skLineSegment(sketch, "E303", {"start": v(49, -20.65) * mm, "end": v(47.5, -20.65) * mm});
            skLineSegment(sketch, "E304", {"start": v(47.5, -20.65) * mm, "end": v(47, -21.15) * mm});
            skLineSegment(sketch, "E305", {"start": v(47, -21.15) * mm, "end": v(47, -93.15) * mm});
            skLineSegment(sketch, "E306", {"start": v(47, -93.15) * mm, "end": v(47.5, -93.65) * mm});
            skLineSegment(sketch, "E307", {"start": v(47.5, -93.65) * mm, "end": v(49, -93.65) * mm});
            skLineSegment(sketch, "E308", {"start": v(49, -93.65) * mm, "end": v(49, -96.65) * mm});
            skLineSegment(sketch, "E309", {"start": v(49, -96.65) * mm, "end": v(47.5, -96.65) * mm});
            skLineSegment(sketch, "E310", {"start": v(47.5, -96.65) * mm, "end": v(47, -97.15) * mm});
            skLineSegment(sketch, "E311", {"start": v(47, -97.15) * mm, "end": v(47, -101.69) * mm});
            skArc(sketch, "E312", {"start": v(47, -101.69) * mm, "mid": v(47.07, -101.94) * mm, "end": v(47.25, -102.12) * mm});
            skArc(sketch, "E313", {"start": v(46.57, -102.8) * mm, "mid": v(47.35, -102.9) * mm, "end": v(47.25, -102.12) * mm});
            skArc(sketch, "E314", {"start": v(46.57, -102.8) * mm, "mid": v(46.38, -102.62) * mm, "end": v(46.13, -102.55) * mm});
            skLineSegment(sketch, "E315", {"start": v(46.13, -102.55) * mm, "end": v(44.5, -102.55) * mm});
            skArc(sketch, "E316", {"start": v(44.5, -102.55) * mm, "mid": v(44.15, -102.7) * mm, "end": v(44, -103.05) * mm});
            skLineSegment(sketch, "E317", {"start": v(44, -103.05) * mm, "end": v(44, -108.05) * mm});
            skArc(sketch, "E318", {"start": v(44, -108.05) * mm, "mid": v(44.15, -108.4) * mm, "end": v(44.5, -108.55) * mm});
            skLineSegment(sketch, "E319", {"start": v(44.5, -108.55) * mm, "end": v(46.13, -108.55) * mm});
            skArc(sketch, "E320", {"start": v(46.13, -108.55) * mm, "mid": v(46.38, -108.49) * mm, "end": v(46.57, -108.3) * mm});
            skArc(sketch, "E321", {"start": v(47.25, -108.99) * mm, "mid": v(47.35, -108.2) * mm, "end": v(46.57, -108.3) * mm});
            skArc(sketch, "E322", {"start": v(47.25, -108.99) * mm, "mid": v(47.07, -109.17) * mm, "end": v(47, -109.42) * mm});
            skLineSegment(sketch, "E323", {"start": v(47, -109.42) * mm, "end": v(47, -114.55) * mm});
            skLineSegment(sketch, "E324", {"start": v(47, -114.55) * mm, "end": v(50, -114.55) * mm});
            skLineSegment(sketch, "E325", {"start": v(50, -114.55) * mm, "end": v(50, -113.28) * mm});
            skLineSegment(sketch, "E326", {"start": v(50, -113.28) * mm, "end": v(54, -113.28) * mm});
            skLineSegment(sketch, "E327", {"start": v(54, -113.28) * mm, "end": v(54, -114.55) * mm});
            skLineSegment(sketch, "E328", {"start": v(54, -114.55) * mm, "end": v(57, -114.55) * mm});
            skLineSegment(sketch, "E329", {"start": v(57, -114.55) * mm, "end": v(57, -117.75) * mm});
            skLineSegment(sketch, "E330", {"start": v(57, -117.75) * mm, "end": v(54, -117.75) * mm});
            skLineSegment(sketch, "E331", {"start": v(54, -117.75) * mm, "end": v(54, -119.03) * mm});
            skLineSegment(sketch, "E332", {"start": v(54, -119.03) * mm, "end": v(50, -119.03) * mm});
            skLineSegment(sketch, "E333", {"start": v(50, -119.03) * mm, "end": v(50, -117.75) * mm});
            skLineSegment(sketch, "E334", {"start": v(50, -117.75) * mm, "end": v(47, -117.75) * mm});
            skLineSegment(sketch, "E335", {"start": v(47, -117.75) * mm, "end": v(47, -122.89) * mm});
            skArc(sketch, "E336", {"start": v(47, -122.89) * mm, "mid": v(47.07, -123.14) * mm, "end": v(47.25, -123.32) * mm});
            skArc(sketch, "E337", {"start": v(46.57, -124) * mm, "mid": v(47.35, -124.1) * mm, "end": v(47.25, -123.32) * mm});
            skArc(sketch, "E338", {"start": v(46.57, -124) * mm, "mid": v(46.38, -123.82) * mm, "end": v(46.13, -123.75) * mm});
            skLineSegment(sketch, "E339", {"start": v(46.13, -123.75) * mm, "end": v(44.5, -123.75) * mm});
            skArc(sketch, "E340", {"start": v(44.5, -123.75) * mm, "mid": v(44.15, -123.9) * mm, "end": v(44, -124.25) * mm});
            skLineSegment(sketch, "E341", {"start": v(44, -124.25) * mm, "end": v(44, -129.25) * mm});
            skArc(sketch, "E342", {"start": v(44, -129.25) * mm, "mid": v(44.15, -129.6) * mm, "end": v(44.5, -129.75) * mm});
            skLineSegment(sketch, "E343", {"start": v(44.5, -129.75) * mm, "end": v(46.13, -129.75) * mm});
            skArc(sketch, "E344", {"start": v(46.13, -129.75) * mm, "mid": v(46.38, -129.69) * mm, "end": v(46.57, -129.5) * mm});
            skArc(sketch, "E345", {"start": v(47.25, -130.19) * mm, "mid": v(47.35, -129.4) * mm, "end": v(46.57, -129.5) * mm});
            skArc(sketch, "E346", {"start": v(47.25, -130.19) * mm, "mid": v(47.07, -130.37) * mm, "end": v(47, -130.62) * mm});
            skLineSegment(sketch, "E347", {"start": v(47, -130.62) * mm, "end": v(47, -141.69) * mm});
            skArc(sketch, "E348", {"start": v(47, -141.69) * mm, "mid": v(47.07, -141.94) * mm, "end": v(47.25, -142.12) * mm});
            skArc(sketch, "E349", {"start": v(46.57, -142.8) * mm, "mid": v(47.35, -142.9) * mm, "end": v(47.25, -142.12) * mm});
            skArc(sketch, "E350", {"start": v(46.57, -142.8) * mm, "mid": v(46.38, -142.62) * mm, "end": v(46.13, -142.55) * mm});
            skLineSegment(sketch, "E351", {"start": v(46.13, -142.55) * mm, "end": v(-179.5, -142.55) * mm});
            skArc(sketch, "E352", {"start": v(-179.5, -142.55) * mm, "mid": v(-179.85, -142.7) * mm, "end": v(-180, -143.05) * mm});
            skLineSegment(sketch, "E353", {"start": v(-180, -143.05) * mm, "end": v(-180, -148.05) * mm});
            skArc(sketch, "E354", {"start": v(-180, -148.05) * mm, "mid": v(-179.85, -148.4) * mm, "end": v(-179.5, -148.55) * mm});
            skLineSegment(sketch, "E355", {"start": v(-179.5, -148.55) * mm, "end": v(-177.87, -148.55) * mm});
            skArc(sketch, "E356", {"start": v(-177.87, -148.55) * mm, "mid": v(-177.62, -148.49) * mm, "end": v(-177.43, -148.3) * mm});
            skArc(sketch, "E357", {"start": v(-176.75, -148.99) * mm, "mid": v(-176.65, -148.2) * mm, "end": v(-177.43, -148.3) * mm});
            skArc(sketch, "E358", {"start": v(-176.75, -148.99) * mm, "mid": v(-176.93, -149.17) * mm, "end": v(-177, -149.42) * mm});
            skLineSegment(sketch, "E359", {"start": v(-177, -149.42) * mm, "end": v(-177, -154.55) * mm});
            skLineSegment(sketch, "E360", {"start": v(-177, -154.55) * mm, "end": v(-174, -154.55) * mm});
            skLineSegment(sketch, "E361", {"start": v(-174, -154.55) * mm, "end": v(-174, -153.28) * mm});
            skLineSegment(sketch, "E362", {"start": v(-174, -153.28) * mm, "end": v(-170, -153.28) * mm});
            skLineSegment(sketch, "E363", {"start": v(-170, -153.28) * mm, "end": v(-170, -154.55) * mm});
            skLineSegment(sketch, "E364", {"start": v(-170, -154.55) * mm, "end": v(-167, -154.55) * mm});
            skLineSegment(sketch, "E365", {"start": v(-167, -154.55) * mm, "end": v(-167, -157.75) * mm});
            skLineSegment(sketch, "E366", {"start": v(-167, -157.75) * mm, "end": v(-170, -157.75) * mm});
            skLineSegment(sketch, "E367", {"start": v(-170, -157.75) * mm, "end": v(-170, -159.03) * mm});
            skLineSegment(sketch, "E368", {"start": v(-170, -159.03) * mm, "end": v(-174, -159.03) * mm});
            skLineSegment(sketch, "E369", {"start": v(-174, -159.03) * mm, "end": v(-174, -157.75) * mm});
            skLineSegment(sketch, "E370", {"start": v(-174, -157.75) * mm, "end": v(-177, -157.75) * mm});
            skLineSegment(sketch, "E371", {"start": v(-177, -157.75) * mm, "end": v(-177, -162.89) * mm});
            skArc(sketch, "E372", {"start": v(-177, -162.89) * mm, "mid": v(-176.93, -163.14) * mm, "end": v(-176.75, -163.32) * mm});
            skArc(sketch, "E373", {"start": v(-177.43, -164) * mm, "mid": v(-176.65, -164.1) * mm, "end": v(-176.75, -163.32) * mm});
            skArc(sketch, "E374", {"start": v(-177.43, -164) * mm, "mid": v(-177.62, -163.82) * mm, "end": v(-177.87, -163.75) * mm});
            skLineSegment(sketch, "E375", {"start": v(-177.87, -163.75) * mm, "end": v(-179.5, -163.75) * mm});
            skArc(sketch, "E376", {"start": v(-179.5, -163.75) * mm, "mid": v(-179.85, -163.9) * mm, "end": v(-180, -164.25) * mm});
            skLineSegment(sketch, "E377", {"start": v(-180, -164.25) * mm, "end": v(-180, -169.25) * mm});
            skArc(sketch, "E378", {"start": v(-180, -169.25) * mm, "mid": v(-179.85, -169.6) * mm, "end": v(-179.5, -169.75) * mm});
            skLineSegment(sketch, "E379", {"start": v(-179.5, -169.75) * mm, "end": v(46.13, -169.75) * mm});
            skArc(sketch, "E380", {"start": v(46.13, -169.75) * mm, "mid": v(46.38, -169.69) * mm, "end": v(46.57, -169.5) * mm});
            skCircle(sketch, "E381", {"center": v(-16, -156.15) * mm, "radius": 1.6 * mm});
            skCircle(sketch, "E382", {"center": v(54, -19.15) * mm, "radius": 1.55 * mm});
            skCircle(sketch, "E383", {"center": v(54, 83.85) * mm, "radius": 1.55 * mm});
            skLineSegment(sketch, "E384", {"start": v(58, 147.85) * mm, "end": v(78, 147.85) * mm});
            skArc(sketch, "E385", {"start": v(58, 155.85) * mm, "mid": v(54, 151.85) * mm, "end": v(58, 147.85) * mm});
            skLineSegment(sketch, "E386", {"start": v(78, 155.85) * mm, "end": v(58, 155.85) * mm});
            skArc(sketch, "E387", {"start": v(78, 147.85) * mm, "mid": v(82, 151.85) * mm, "end": v(78, 155.85) * mm});
            skCircle(sketch, "E388", {"center": v(120, -123.15) * mm, "radius": 1.55 * mm});
            skCircle(sketch, "E389", {"center": v(150, -123.15) * mm, "radius": 1.55 * mm});
            skCircle(sketch, "E390", {"center": v(90, -123.15) * mm, "radius": 1.55 * mm});
            skLineSegment(sketch, "E391", {"start": v(155, -165.15) * mm, "end": v(142, -165.15) * mm});
            skArc(sketch, "E392", {"start": v(155, -173.15) * mm, "mid": v(159, -169.15) * mm, "end": v(155, -165.15) * mm});
            skLineSegment(sketch, "E393", {"start": v(142, -173.15) * mm, "end": v(155, -173.15) * mm});
            skArc(sketch, "E394", {"start": v(142, -165.15) * mm, "mid": v(138, -169.15) * mm, "end": v(142, -173.15) * mm});
            skLineSegment(sketch, "E395", {"start": v(109.5, -156.94) * mm, "end": v(109.5, -155.37) * mm});
            skArc(sketch, "E396", {"start": v(109.5, -156.94) * mm, "mid": v(109.57, -157.19) * mm, "end": v(109.75, -157.37) * mm});
            skArc(sketch, "E397", {"start": v(109.07, -158.05) * mm, "mid": v(109.85, -158.16) * mm, "end": v(109.75, -157.37) * mm});
            skArc(sketch, "E398", {"start": v(109.07, -158.05) * mm, "mid": v(108.88, -157.87) * mm, "end": v(108.63, -157.8) * mm});
            skLineSegment(sketch, "E399", {"start": v(104.17, -157.8) * mm, "end": v(108.63, -157.8) * mm});
            skArc(sketch, "E400", {"start": v(104.17, -157.8) * mm, "mid": v(103.92, -157.87) * mm, "end": v(103.73, -158.05) * mm});
            skArc(sketch, "E401", {"start": v(103.05, -157.37) * mm, "mid": v(102.95, -158.16) * mm, "end": v(103.73, -158.05) * mm});
            skArc(sketch, "E402", {"start": v(103.05, -157.37) * mm, "mid": v(103.23, -157.19) * mm, "end": v(103.3, -156.94) * mm});
            skLineSegment(sketch, "E403", {"start": v(103.3, -155.37) * mm, "end": v(103.3, -156.94) * mm});
            skArc(sketch, "E404", {"start": v(103.3, -155.37) * mm, "mid": v(103.23, -155.12) * mm, "end": v(103.05, -154.94) * mm});
            skArc(sketch, "E405", {"start": v(103.73, -154.25) * mm, "mid": v(102.95, -154.15) * mm, "end": v(103.05, -154.94) * mm});
            skArc(sketch, "E406", {"start": v(103.73, -154.25) * mm, "mid": v(103.92, -154.44) * mm, "end": v(104.17, -154.5) * mm});
            skLineSegment(sketch, "E407", {"start": v(108.63, -154.5) * mm, "end": v(104.17, -154.5) * mm});
            skArc(sketch, "E408", {"start": v(108.63, -154.5) * mm, "mid": v(108.88, -154.44) * mm, "end": v(109.07, -154.25) * mm});
            skArc(sketch, "E409", {"start": v(109.75, -154.94) * mm, "mid": v(109.85, -154.15) * mm, "end": v(109.07, -154.25) * mm});
            skArc(sketch, "E410", {"start": v(109.75, -154.94) * mm, "mid": v(109.57, -155.12) * mm, "end": v(109.5, -155.37) * mm});
            skLineSegment(sketch, "E411", {"start": v(130.7, -156.94) * mm, "end": v(130.7, -155.37) * mm});
            skArc(sketch, "E412", {"start": v(130.7, -156.94) * mm, "mid": v(130.77, -157.19) * mm, "end": v(130.95, -157.37) * mm});
            skArc(sketch, "E413", {"start": v(130.27, -158.05) * mm, "mid": v(131.05, -158.16) * mm, "end": v(130.95, -157.37) * mm});
            skArc(sketch, "E414", {"start": v(130.27, -158.05) * mm, "mid": v(130.08, -157.87) * mm, "end": v(129.83, -157.8) * mm});
            skLineSegment(sketch, "E415", {"start": v(125.37, -157.8) * mm, "end": v(129.83, -157.8) * mm});
            skArc(sketch, "E416", {"start": v(125.37, -157.8) * mm, "mid": v(125.12, -157.87) * mm, "end": v(124.93, -158.05) * mm});
            skArc(sketch, "E417", {"start": v(124.25, -157.37) * mm, "mid": v(124.15, -158.16) * mm, "end": v(124.93, -158.05) * mm});
            skArc(sketch, "E418", {"start": v(124.25, -157.37) * mm, "mid": v(124.43, -157.19) * mm, "end": v(124.5, -156.94) * mm});
            skLineSegment(sketch, "E419", {"start": v(124.5, -155.37) * mm, "end": v(124.5, -156.94) * mm});
            skArc(sketch, "E420", {"start": v(124.5, -155.37) * mm, "mid": v(124.43, -155.12) * mm, "end": v(124.25, -154.94) * mm});
            skArc(sketch, "E421", {"start": v(124.93, -154.25) * mm, "mid": v(124.15, -154.15) * mm, "end": v(124.25, -154.94) * mm});
            skArc(sketch, "E422", {"start": v(124.93, -154.25) * mm, "mid": v(125.12, -154.44) * mm, "end": v(125.37, -154.5) * mm});
            skLineSegment(sketch, "E423", {"start": v(129.83, -154.5) * mm, "end": v(125.37, -154.5) * mm});
            skArc(sketch, "E424", {"start": v(129.83, -154.5) * mm, "mid": v(130.08, -154.44) * mm, "end": v(130.27, -154.25) * mm});
            skArc(sketch, "E425", {"start": v(130.95, -154.94) * mm, "mid": v(131.05, -154.15) * mm, "end": v(130.27, -154.25) * mm});
            skArc(sketch, "E426", {"start": v(130.95, -154.94) * mm, "mid": v(130.77, -155.12) * mm, "end": v(130.7, -155.37) * mm});
            skCircle(sketch, "E427", {"center": v(152, -141.15) * mm, "radius": 1.6 * mm});
            skLineSegment(sketch, "E428", {"start": v(142.2, 41.85) * mm, "end": v(142.2, 121.85) * mm});
            skArc(sketch, "E429", {"start": v(137.8, 41.85) * mm, "mid": v(140, 39.65) * mm, "end": v(142.2, 41.85) * mm});
            skLineSegment(sketch, "E430", {"start": v(137.8, 121.85) * mm, "end": v(137.8, 41.85) * mm});
            skArc(sketch, "E431", {"start": v(142.2, 121.85) * mm, "mid": v(140, 124.05) * mm, "end": v(137.8, 121.85) * mm});
            skLineSegment(sketch, "E432", {"start": v(92.2, 41.85) * mm, "end": v(92.2, 121.85) * mm});
            skArc(sketch, "E433", {"start": v(87.8, 41.85) * mm, "mid": v(90, 39.65) * mm, "end": v(92.2, 41.85) * mm});
            skLineSegment(sketch, "E434", {"start": v(87.8, 121.85) * mm, "end": v(87.8, 41.85) * mm});
            skArc(sketch, "E435", {"start": v(92.2, 121.85) * mm, "mid": v(90, 124.05) * mm, "end": v(87.8, 121.85) * mm});
            skLineSegment(sketch, "E436", {"start": v(151, 18.85) * mm, "end": v(163, 18.85) * mm});
            skArc(sketch, "E437", {"start": v(147, 22.85) * mm, "mid": v(148.17, 20.02) * mm, "end": v(151, 18.85) * mm});
            skLineSegment(sketch, "E438", {"start": v(147, 114.85) * mm, "end": v(147, 22.85) * mm});
            skArc(sketch, "E439", {"start": v(151, 118.85) * mm, "mid": v(148.17, 117.68) * mm, "end": v(147, 114.85) * mm});
            skLineSegment(sketch, "E440", {"start": v(163, 118.85) * mm, "end": v(151, 118.85) * mm});
            skArc(sketch, "E441", {"start": v(167, 114.85) * mm, "mid": v(165.83, 117.68) * mm, "end": v(163, 118.85) * mm});
            skLineSegment(sketch, "E442", {"start": v(167, 22.85) * mm, "end": v(167, 114.85) * mm});
            skArc(sketch, "E443", {"start": v(163, 18.85) * mm, "mid": v(165.83, 20.02) * mm, "end": v(167, 22.85) * mm});
            skLineSegment(sketch, "E444", {"start": v(147, 0.85) * mm, "end": v(147, -91.15) * mm});
            skArc(sketch, "E445", {"start": v(151, 4.85) * mm, "mid": v(148.17, 3.68) * mm, "end": v(147, 0.85) * mm});
            skLineSegment(sketch, "E446", {"start": v(163, 4.85) * mm, "end": v(151, 4.85) * mm});
            skArc(sketch, "E447", {"start": v(167, 0.85) * mm, "mid": v(165.83, 3.68) * mm, "end": v(163, 4.85) * mm});
            skLineSegment(sketch, "E448", {"start": v(167, -91.15) * mm, "end": v(167, 0.85) * mm});
            skArc(sketch, "E449", {"start": v(163, -95.15) * mm, "mid": v(165.83, -93.98) * mm, "end": v(167, -91.15) * mm});
            skLineSegment(sketch, "E450", {"start": v(151, -95.15) * mm, "end": v(163, -95.15) * mm});
            skArc(sketch, "E451", {"start": v(147, -91.15) * mm, "mid": v(148.17, -93.98) * mm, "end": v(151, -95.15) * mm});
            skLineSegment(sketch, "E452", {"start": v(83, 22.85) * mm, "end": v(83, 114.85) * mm});
            skArc(sketch, "E453", {"start": v(79, 18.85) * mm, "mid": v(81.83, 20.02) * mm, "end": v(83, 22.85) * mm});
            skLineSegment(sketch, "E454", {"start": v(67, 18.85) * mm, "end": v(79, 18.85) * mm});
            skArc(sketch, "E455", {"start": v(63, 22.85) * mm, "mid": v(64.17, 20.02) * mm, "end": v(67, 18.85) * mm});
            skLineSegment(sketch, "E456", {"start": v(63, 114.85) * mm, "end": v(63, 22.85) * mm});
            skArc(sketch, "E457", {"start": v(67, 118.85) * mm, "mid": v(64.17, 117.68) * mm, "end": v(63, 114.85) * mm});
            skLineSegment(sketch, "E458", {"start": v(79, 118.85) * mm, "end": v(67, 118.85) * mm});
            skArc(sketch, "E459", {"start": v(83, 114.85) * mm, "mid": v(81.83, 117.68) * mm, "end": v(79, 118.85) * mm});
            skLineSegment(sketch, "E460", {"start": v(79, 4.85) * mm, "end": v(67, 4.85) * mm});
            skArc(sketch, "E461", {"start": v(83, 0.85) * mm, "mid": v(81.83, 3.68) * mm, "end": v(79, 4.85) * mm});
            skLineSegment(sketch, "E462", {"start": v(83, -91.15) * mm, "end": v(83, 0.85) * mm});
            skArc(sketch, "E463", {"start": v(79, -95.15) * mm, "mid": v(81.83, -93.98) * mm, "end": v(83, -91.15) * mm});
            skLineSegment(sketch, "E464", {"start": v(67, -95.15) * mm, "end": v(79, -95.15) * mm});
            skArc(sketch, "E465", {"start": v(63, -91.15) * mm, "mid": v(64.17, -93.98) * mm, "end": v(67, -95.15) * mm});
            skLineSegment(sketch, "E466", {"start": v(63, 0.85) * mm, "end": v(63, -91.15) * mm});
            skArc(sketch, "E467", {"start": v(67, 4.85) * mm, "mid": v(64.17, 3.68) * mm, "end": v(63, 0.85) * mm});
            skLineSegment(sketch, "E468", {"start": v(133, 22.85) * mm, "end": v(133, 114.85) * mm});
            skArc(sketch, "E469", {"start": v(129, 18.85) * mm, "mid": v(131.83, 20.02) * mm, "end": v(133, 22.85) * mm});
            skLineSegment(sketch, "E470", {"start": v(101, 18.85) * mm, "end": v(129, 18.85) * mm});
            skArc(sketch, "E471", {"start": v(97, 22.85) * mm, "mid": v(98.17, 20.02) * mm, "end": v(101, 18.85) * mm});
            skLineSegment(sketch, "E472", {"start": v(97, 114.85) * mm, "end": v(97, 22.85) * mm});
            skArc(sketch, "E473", {"start": v(101, 118.85) * mm, "mid": v(98.17, 117.68) * mm, "end": v(97, 114.85) * mm});
            skLineSegment(sketch, "E474", {"start": v(129, 118.85) * mm, "end": v(101, 118.85) * mm});
            skArc(sketch, "E475", {"start": v(133, 114.85) * mm, "mid": v(131.83, 117.68) * mm, "end": v(129, 118.85) * mm});
            skLineSegment(sketch, "E476", {"start": v(129, 4.85) * mm, "end": v(101, 4.85) * mm});
            skArc(sketch, "E477", {"start": v(133, 0.85) * mm, "mid": v(131.83, 3.68) * mm, "end": v(129, 4.85) * mm});
            skLineSegment(sketch, "E478", {"start": v(133, -91.15) * mm, "end": v(133, 0.85) * mm});
            skArc(sketch, "E479", {"start": v(129, -95.15) * mm, "mid": v(131.83, -93.98) * mm, "end": v(133, -91.15) * mm});
            skLineSegment(sketch, "E480", {"start": v(101, -95.15) * mm, "end": v(129, -95.15) * mm});
            skArc(sketch, "E481", {"start": v(97, -91.15) * mm, "mid": v(98.17, -93.98) * mm, "end": v(101, -95.15) * mm});
            skLineSegment(sketch, "E482", {"start": v(97, 0.85) * mm, "end": v(97, -91.15) * mm});
            skArc(sketch, "E483", {"start": v(101, 4.85) * mm, "mid": v(98.17, 3.68) * mm, "end": v(97, 0.85) * mm});
            skCircle(sketch, "E484", {"center": v(67, 141.85) * mm, "radius": 1.55 * mm});
            skCircle(sketch, "E485", {"center": v(90, 141.85) * mm, "radius": 1.55 * mm});
            skCircle(sketch, "E486", {"center": v(120, 141.85) * mm, "radius": 1.55 * mm});
            skCircle(sketch, "E487", {"center": v(150, 141.85) * mm, "radius": 1.55 * mm});
            skCircle(sketch, "E488", {"center": v(-117, -156.15) * mm, "radius": 1.6 * mm});
            skCircle(sketch, "E489", {"center": v(-103.25, -165.45) * mm, "radius": 1.55 * mm});
            skCircle(sketch, "E490", {"center": v(-29.25, -165.45) * mm, "radius": 1.55 * mm});
            skCircle(sketch, "E491", {"center": v(-163.25, -146.86) * mm, "radius": 1.55 * mm});
            skCircle(sketch, "E492", {"center": v(-29.25, -146.86) * mm, "radius": 1.55 * mm});
            skSolve(sketch);
        }
        {
            var Q0;
            Q0=qSketchRegion(id+"F0",true);
            extrude(context, id + "F1", {"entities" : qUnion([Q0]), "depth" : 3 * mm, "offsetDistance" : 25 * mm});
        }
    });
